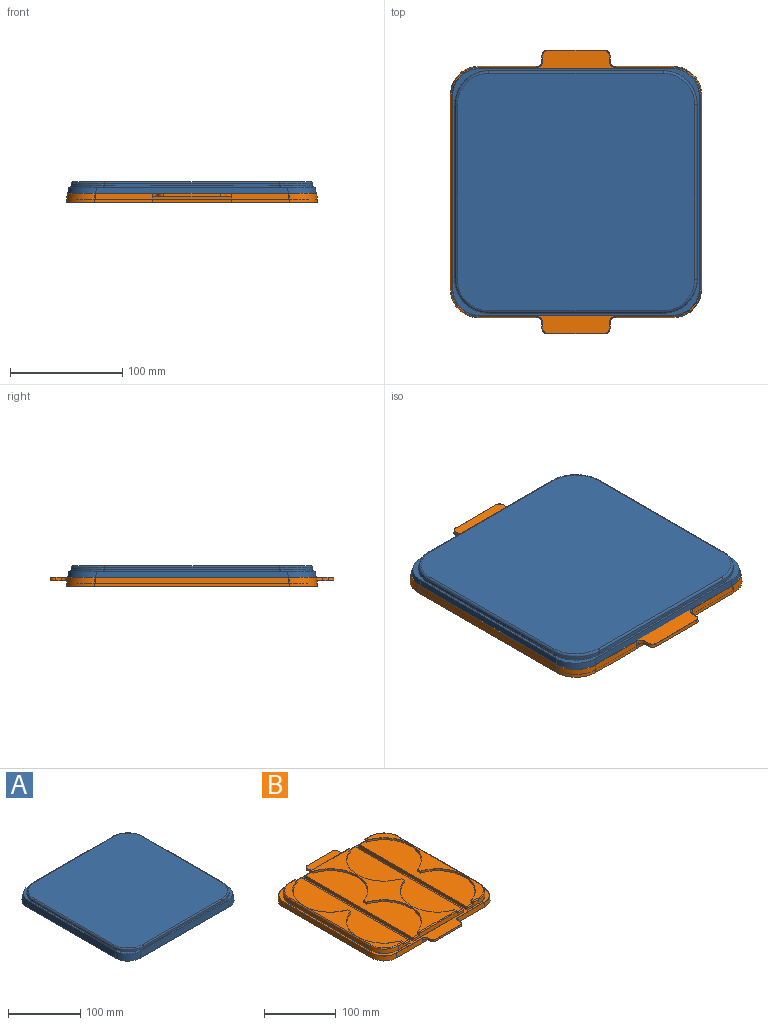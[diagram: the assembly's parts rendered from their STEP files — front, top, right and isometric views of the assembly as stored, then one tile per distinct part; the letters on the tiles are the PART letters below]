
ASSEMBLY  parts=2 mates=1
PART A: 45 faces, bbox 222.6x222.6x17.1 mm
  f0: plane 222.4x222.4mm, normal (0,0,-1), area 2110.5mm2, adj f2,f3,f4,f5,f6,f7,f8,f9
  f1: plane 220.09x220.09mm, normal (0,0,1), area 1993.2mm2, adj f2,f3,f4,f5,f6,f7,f8,f9
  f2: plane 172.67x11mm, normal (0,0.99,0.1), area 1897.1mm2, adj f0,f1,f6,f9
  f3: plane 172.67x11mm, normal (-0.99,0,0.1), area 1897.1mm2, adj f0,f1,f6,f7
  f4: plane 172.67x11mm, normal (0,-0.99,0.1), area 1897.1mm2, adj f0,f1,f7,f8
  f5: plane 172.67x11mm, normal (0.99,0,0.1), area 1897.1mm2, adj f0,f1,f8,f9
  f6: cylinder r=25mm len=26.13mm, axis (-0.1,0.1,-0.99), area 433.7mm2, adj f0,f1,f2,f3
  f7: cylinder r=25mm len=26.13mm, axis (-0.1,-0.1,-0.99), area 433.7mm2, adj f0,f1,f3,f4
  f8: cylinder r=25mm len=26.13mm, axis (0.1,-0.1,-0.99), area 433.7mm2, adj f0,f1,f4,f5
  f9: cylinder r=25mm len=26.13mm, axis (0.1,0.1,-0.99), area 433.7mm2, adj f0,f1,f2,f5
  f10: plane 156.38x3.21mm, normal (0,0.99,0.1), area 503.5mm2, adj f1,f15,f18,f24
  f11: plane 156.38x3.21mm, normal (-0.99,0,0.1), area 503.5mm2, adj f1,f15,f16,f25
  f12: plane 156.38x3.21mm, normal (0,-0.99,0.1), area 503.5mm2, adj f1,f16,f17,f21
  f13: plane 156.38x3.21mm, normal (0.99,0,0.1), area 503.5mm2, adj f1,f17,f18,f20
  f14: plane 211.4x211.4mm, normal (0,0,1), area 44026mm2, adj f19,f20,f21,f22,f23,f24,f25,f26
  f15: cylinder r=30mm len=30.31mm, axis (0.1,-0.1,0.99), area 154.5mm2, adj f1,f10,f11,f26
  f16: cylinder r=30mm len=30.31mm, axis (0.1,0.1,0.99), area 154.5mm2, adj f1,f11,f12,f23
  f17: cylinder r=30mm len=30.31mm, axis (-0.1,0.1,0.99), area 154.5mm2, adj f1,f12,f13,f19
  f18: cylinder r=30mm len=30.31mm, axis (-0.1,-0.1,0.99), area 154.5mm2, adj f1,f10,f13,f22
  f19: bspline ~29.84x29.84mm, area 131.3mm2, adj f14,f17,f20,f21
  f20: cylinder r=2mm len=155.71mm, axis (0,-1,0), area 456.6mm2, adj f13,f14,f19,f22
  f21: cylinder r=2mm len=155.71mm, axis (1,0,0), area 456.6mm2, adj f12,f14,f19,f23
  f22: bspline ~29.84x29.84mm, area 131.3mm2, adj f14,f18,f20,f24
  f23: bspline ~29.84x29.84mm, area 131.3mm2, adj f14,f16,f21,f25
  f24: cylinder r=2mm len=155.71mm, axis (1,0,0), area 456.6mm2, adj f10,f14,f22,f26
  f25: cylinder r=2mm len=155.71mm, axis (0,-1,0), area 456.6mm2, adj f11,f14,f23,f26
  f26: bspline ~29.84x29.84mm, area 131.3mm2, adj f14,f15,f24,f25
  f27: plane 215.59x215.59mm, normal (0,0,-1), area 1935.7mm2, adj f28,f29,f30,f31,f32,f33,f34,f35
  f28: plane 172.62x8.5mm, normal (0,-0.99,-0.1), area 1467.7mm2, adj f0,f27,f32,f35
  f29: plane 172.62x8.5mm, normal (0.99,0,-0.1), area 1467.7mm2, adj f0,f27,f32,f33
  f30: plane 172.62x8.5mm, normal (0,0.99,-0.1), area 1467.7mm2, adj f0,f27,f33,f34
  f31: plane 172.62x8.5mm, normal (-0.99,0,-0.1), area 1467.7mm2, adj f0,f27,f34,f35
  f32: cylinder r=22.5mm len=23.37mm, axis (-0.1,0.1,-0.99), area 301.6mm2, adj f0,f27,f28,f29
  f33: cylinder r=22.5mm len=23.37mm, axis (-0.1,-0.1,-0.99), area 301.6mm2, adj f0,f27,f29,f30
  f34: cylinder r=22.5mm len=23.37mm, axis (0.1,-0.1,-0.99), area 301.6mm2, adj f0,f27,f30,f31
  f35: cylinder r=22.5mm len=23.37mm, axis (0.1,0.1,-0.99), area 301.6mm2, adj f0,f27,f28,f31
  f36: plane 156.85x5mm, normal (0,-0.99,-0.1), area 785.9mm2, adj f27,f40,f41,f44
  f37: plane 156.85x5mm, normal (0.99,0,-0.1), area 785.9mm2, adj f27,f40,f41,f42
  f38: plane 156.85x5mm, normal (0,0.99,-0.1), area 785.9mm2, adj f27,f40,f42,f43
  f39: plane 156.85x5mm, normal (-0.99,0,-0.1), area 785.9mm2, adj f27,f40,f43,f44
  f40: plane 210.5x210.5mm, normal (0,0,-1), area 43669.6mm2, adj f36,f37,f38,f39,f41,f42,f43,f44
  f41: cylinder r=27.5mm len=28mm, axis (0.1,-0.1,0.99), area 216.8mm2, adj f27,f36,f37,f40
  f42: cylinder r=27.5mm len=28mm, axis (0.1,0.1,0.99), area 216.8mm2, adj f27,f37,f38,f40
  f43: cylinder r=27.5mm len=28mm, axis (-0.1,0.1,0.99), area 216.8mm2, adj f27,f38,f39,f40
  f44: cylinder r=27.5mm len=28mm, axis (-0.1,-0.1,0.99), area 216.8mm2, adj f27,f36,f39,f40
PART B: 298 faces, bbox 224x253.1x16.9 mm
  f0: plane 45.03x40.25mm, normal (0,0,-1), area 1431.9mm2, adj f1,f2,f130,f146,f213
  f1: plane 16.07x8.03mm, normal (-1,0,-0.09), area 100.6mm2, adj f0,f127,f139,f146,f163,f213
  f2: plane 40.95x5mm, normal (1,0,-0.09), area 203.8mm2, adj f0,f130,f139,f213
  f3: plane 93.03x40.25mm, normal (0,0,-1), area 2878.5mm2, adj f4,f5,f111,f116,f117,f211
  f4: plane 40.95x5mm, normal (1,0,-0.09), area 203.8mm2, adj f3,f111,f139,f211
  f5: plane 40.95x5mm, normal (-1,0,-0.09), area 203.8mm2, adj f3,f111,f139,f211
  f6: plane 16.07x8.03mm, normal (1,0,-0.09), area 100.6mm2, adj f7,f122,f135,f139,f160,f209
  f7: plane 45.03x40.25mm, normal (0,0,-1), area 1431.9mm2, adj f6,f8,f122,f133,f209
  f8: plane 40.95x5mm, normal (-1,0,-0.09), area 203.8mm2, adj f7,f133,f139,f209
  f9: plane 45.03x17.19mm, normal (0,0,-1), area 774.1mm2, adj f10,f11,f207,f283,f284,f285
  f10: plane 17.7x5mm, normal (-1,0,-0.09), area 87.5mm2, adj f9,f139,f207,f283
  f11: plane 17.7x5mm, normal (1,0,-0.09), area 87.5mm2, adj f9,f139,f207,f284
  f12: plane 93.03x17.19mm, normal (0,0,-1), area 1599.2mm2, adj f13,f14,f205,f280,f281,f282
  f13: plane 17.7x5mm, normal (1,0,-0.09), area 87.5mm2, adj f12,f139,f205,f281
  f14: plane 17.7x5mm, normal (-1,0,-0.09), area 87.5mm2, adj f12,f139,f205,f280
  f15: plane 17.7x5mm, normal (1,0,-0.09), area 87.5mm2, adj f16,f139,f203,f288
  f16: plane 45.03x17.19mm, normal (0,0,-1), area 774.1mm2, adj f15,f17,f203,f286,f287,f288
  f17: plane 17.7x5mm, normal (-1,0,-0.09), area 87.5mm2, adj f16,f139,f203,f286
  f18: plane 82.91x45.03mm, normal (0,0,-1), area 2873.8mm2, adj f19,f20,f121,f144,f145,f265,f266,f267
  f19: plane 83.43x8.03mm, normal (-1,0,-0.09), area 620.6mm2, adj f18,f121,f126,f139,f144,f265,f297
  f20: plane 83.4x5mm, normal (1,0,-0.09), area 417.3mm2, adj f18,f139,f266,f295
  f21: plane 93.03x82.91mm, normal (0,0,-1), area 5775.4mm2, adj f22,f23,f118,f119,f147,f148,f150,f151
  f22: plane 83.4x5mm, normal (1,0,-0.09), area 417.3mm2, adj f21,f139,f263,f294
  f23: plane 83.4x5mm, normal (-1,0,-0.09), area 417.3mm2, adj f21,f139,f262,f292
  f24: plane 83.43x8.03mm, normal (1,0,-0.09), area 620.6mm2, adj f25,f123,f124,f139,f152,f270,f291
  f25: plane 82.91x45.03mm, normal (0,0,-1), area 2873.8mm2, adj f24,f26,f123,f152,f153,f268,f269,f270
  f26: plane 83.4x5mm, normal (-1,0,-0.09), area 417.3mm2, adj f25,f139,f268,f289
  f27: plane 45.03x40.25mm, normal (0,0,-1), area 1431.9mm2, adj f28,f29,f120,f132,f206
  f28: plane 16.07x8.03mm, normal (-1,0,-0.09), area 100.6mm2, adj f27,f120,f136,f139,f162,f206
  f29: plane 40.95x5mm, normal (1,0,-0.09), area 203.8mm2, adj f27,f132,f139,f206
  f30: plane 93.03x40.25mm, normal (0,0,-1), area 2878.5mm2, adj f31,f32,f131,f149,f155,f204
  f31: plane 40.95x5mm, normal (1,0,-0.09), area 203.8mm2, adj f30,f131,f139,f204
  f32: plane 40.95x5mm, normal (-1,0,-0.09), area 203.8mm2, adj f30,f131,f139,f204
  f33: plane 16.07x8.03mm, normal (1,0,-0.09), area 100.6mm2, adj f34,f125,f139,f154,f161,f202
  f34: plane 45.03x40.25mm, normal (0,0,-1), area 1431.9mm2, adj f33,f35,f134,f154,f202
  f35: plane 40.95x5mm, normal (-1,0,-0.09), area 203.8mm2, adj f34,f134,f139,f202
  f36: plane 51.99x7.82mm, normal (0,1,0.09), area 402.8mm2, adj f56,f87,f178,f187,f224
  f37: plane 51.99x7.82mm, normal (0,-1,0.09), area 402.8mm2, adj f56,f89,f177,f186,f227
  f38: plane 51.99x7.82mm, normal (0,1,0.09), area 402.8mm2, adj f56,f88,f179,f188,f235
  f39: plane 99.37x6.45mm, normal (0,1,0.09), area 567.3mm2, adj f59,f69,f79,f81,f102,f105,f110,f249
  f40: plane 23.47x6.45mm, normal (0,1,0.09), area 112.2mm2, adj f58,f82,f86,f95,f106,f240
  f41: plane 99.37x6.45mm, normal (0,-1,0.09), area 567.3mm2, adj f67,f77,f79,f81,f101,f107,f109,f248
  f42: plane 23.47x6.45mm, normal (0,-1,0.09), area 112.2mm2, adj f60,f82,f85,f91,f108,f238
  f43: plane 211.78x48.25mm, normal (0,0,1), area 7810.2mm2, adj f58,f60,f61,f62,f63,f82,f106,f108
  f44: plane 211.78x48.25mm, normal (0,0,1), area 7810.2mm2, adj f69,f71,f72,f77,f78,f79,f105,f107
  f45: plane 23.47x6.45mm, normal (0,1,0.09), area 112.2mm2, adj f70,f80,f83,f100,f104,f243
  f46: plane 23.47x6.45mm, normal (0,-1,0.09), area 112.2mm2, adj f76,f80,f84,f96,f103,f245
  f47: plane 211.25x36.63mm, normal (0,0,1), area 2103.5mm2, adj f70,f76,f96,f97,f98,f99,f100,f259
  f48: plane 211.25x36.63mm, normal (0,0,1), area 2103.5mm2, adj f58,f60,f91,f92,f93,f94,f95,f250
  f49: plane 159.58x6.45mm, normal (-1,0,0.09), area 1029.3mm2, adj f83,f84,f98,f246
  f50: plane 159.58x6.45mm, normal (1,0,0.09), area 1029.3mm2, adj f85,f86,f93,f241
  f51: plane 211.25x74mm, normal (0,0,1), area 4962.1mm2, adj f59,f67,f69,f77,f109,f110,f253,f254
  f52: plane 252.04x222.03mm, normal (0,0,1), area 7538mm2, adj f79,f80,f81,f82,f214,f215,f216,f217
  f53: plane 173.99x7.82mm, normal (-1,0,0.09), area 1360mm2, adj f56,f87,f90,f220
  f54: plane 173.99x7.82mm, normal (1,0,0.09), area 1360mm2, adj f56,f88,f89,f231
  f55: plane 51.99x7.82mm, normal (0,-1,0.09), area 402.8mm2, adj f56,f90,f176,f184,f216
  f56: plane 223.8x223.8mm, normal (0,0,-1), area 2440.3mm2, adj f36,f37,f38,f53,f54,f55,f87,f88
  f57: plane 211.78x48.25mm, normal (0,0,1), area 7810.2mm2, adj f59,f64,f65,f66,f67,f81,f101,f102
  f58: plane 4.83x4.37mm, normal (-1,0,0.09), area 13.5mm2, adj f40,f43,f48,f63,f95,f106,f250
  f59: plane 4.83x4.37mm, normal (1,0,0.09), area 13.5mm2, adj f39,f51,f57,f64,f102,f110,f255
  f60: plane 4.83x4.37mm, normal (-1,0,0.09), area 13.5mm2, adj f42,f43,f48,f61,f91,f108,f252
  f61: cone r=52.25mm half-angle=5deg, axis (0,0,1), area 371.8mm2, adj f43,f60,f62,f252
  f62: plane 6.9x2.82mm, normal (-1,0,0.09), area 19mm2, adj f43,f61,f63,f251
  f63: cone r=52.25mm half-angle=5deg, axis (0,0,1), area 371.8mm2, adj f43,f58,f62,f250
  f64: cone r=52.25mm half-angle=5deg, axis (0,0,1), area 371.8mm2, adj f57,f59,f65,f255
  f65: plane 6.9x2.82mm, normal (1,0,0.09), area 19mm2, adj f57,f64,f66,f254
  f66: cone r=52.25mm half-angle=5deg, axis (0,0,1), area 371.8mm2, adj f57,f65,f67,f253
  f67: plane 4.83x4.37mm, normal (1,0,0.09), area 13.5mm2, adj f41,f51,f57,f66,f101,f109,f253
  f68: plane 211.78x48.25mm, normal (0,0,1), area 7810.2mm2, adj f70,f73,f74,f75,f76,f80,f103,f104
  f69: plane 4.83x4.37mm, normal (-1,0,0.09), area 13.5mm2, adj f39,f44,f51,f72,f105,f110,f256
  f70: plane 4.83x4.37mm, normal (1,0,0.09), area 13.5mm2, adj f45,f47,f68,f73,f100,f104,f259
  f71: plane 6.9x2.82mm, normal (-1,0,0.09), area 19mm2, adj f44,f72,f78,f257
  f72: cone r=52.25mm half-angle=5deg, axis (0,0,1), area 371.8mm2, adj f44,f69,f71,f256
  f73: cone r=52.25mm half-angle=5deg, axis (0,0,1), area 371.8mm2, adj f68,f70,f74,f259
  f74: plane 6.9x2.82mm, normal (1,0,0.09), area 19mm2, adj f68,f73,f75,f260
  f75: cone r=52.25mm half-angle=5deg, axis (0,0,1), area 371.8mm2, adj f68,f74,f76,f261
  f76: plane 4.83x4.37mm, normal (1,0,0.09), area 13.5mm2, adj f46,f47,f68,f75,f96,f103,f261
  f77: plane 4.83x4.37mm, normal (-1,0,0.09), area 13.5mm2, adj f41,f44,f51,f78,f107,f109,f258
  f78: cone r=52.25mm half-angle=5deg, axis (0,0,1), area 371.8mm2, adj f44,f71,f77,f258
  f79: plane 215.77x5.01mm, normal (-1,0,0.09), area 1078.1mm2, adj f39,f41,f44,f52,f105,f107,f248,f249
  f80: plane 215.77x5.01mm, normal (1,0,0.09), area 1078.1mm2, adj f45,f46,f52,f68,f103,f104,f243,f245
  f81: plane 215.77x5.01mm, normal (1,0,0.09), area 1078.1mm2, adj f39,f41,f52,f57,f101,f102,f248,f249
  f82: plane 215.77x5.01mm, normal (-1,0,0.09), area 1078.1mm2, adj f40,f42,f43,f52,f106,f108,f238,f240
  f83: cylinder r=28mm len=28.55mm, axis (0.09,-0.09,0.99), area 286.1mm2, adj f45,f49,f99,f244
  f84: cylinder r=28mm len=28.55mm, axis (0.09,0.09,0.99), area 286.1mm2, adj f46,f49,f97,f247
  f85: cylinder r=28mm len=28.55mm, axis (-0.09,0.09,0.99), area 286.1mm2, adj f42,f50,f92,f239
  f86: cylinder r=28mm len=28.55mm, axis (-0.09,-0.09,0.99), area 286.1mm2, adj f40,f50,f94,f242
  f87: cylinder r=25mm len=25.67mm, axis (0.09,-0.09,0.99), area 308mm2, adj f36,f53,f56,f222
  f88: cylinder r=25mm len=25.67mm, axis (-0.09,-0.09,0.99), area 308mm2, adj f38,f54,f56,f233
  f89: cylinder r=25mm len=25.67mm, axis (-0.09,0.09,0.99), area 308mm2, adj f37,f54,f56,f229
  f90: cylinder r=25mm len=25.67mm, axis (0.09,0.09,0.99), area 308mm2, adj f53,f55,f56,f218
  f91: cylinder r=1.5mm len=10.35mm, axis (1,0,0), area 22.9mm2, adj f42,f48,f60,f92
  f92: bspline ~27.89x27.89mm, area 94mm2, adj f48,f85,f91,f93
  f93: cylinder r=1.5mm len=158.45mm, axis (0,-1,0), area 352.6mm2, adj f48,f50,f92,f94
  f94: bspline ~27.89x27.89mm, area 94mm2, adj f48,f86,f93,f95
  f95: cylinder r=1.5mm len=10.35mm, axis (1,0,0), area 22.9mm2, adj f40,f48,f58,f94
  f96: cylinder r=1.5mm len=10.35mm, axis (1,0,0), area 22.9mm2, adj f46,f47,f76,f97
  f97: bspline ~27.89x27.89mm, area 94mm2, adj f47,f84,f96,f98
  f98: cylinder r=1.5mm len=158.45mm, axis (0,-1,0), area 352.6mm2, adj f47,f49,f97,f99
  f99: bspline ~27.89x27.89mm, area 94mm2, adj f47,f83,f98,f100
  f100: cylinder r=1.5mm len=10.35mm, axis (1,0,0), area 22.9mm2, adj f45,f47,f70,f99
  f101: cylinder r=1.5mm len=12.12mm, axis (-1,0,0), area 26.7mm2, adj f41,f57,f67,f81
  f102: cylinder r=1.5mm len=12.12mm, axis (-1,0,0), area 26.7mm2, adj f39,f57,f59,f81
  f103: cylinder r=1.5mm len=12.12mm, axis (-1,0,0), area 26.7mm2, adj f46,f68,f76,f80
  f104: cylinder r=1.5mm len=12.12mm, axis (-1,0,0), area 26.7mm2, adj f45,f68,f70,f80
  f105: cylinder r=1.5mm len=12.12mm, axis (-1,0,0), area 26.7mm2, adj f39,f44,f69,f79
  f106: cylinder r=1.5mm len=12.12mm, axis (-1,0,0), area 26.7mm2, adj f40,f43,f58,f82
  f107: cylinder r=1.5mm len=12.12mm, axis (-1,0,0), area 26.7mm2, adj f41,f44,f77,f79
  f108: cylinder r=1.5mm len=12.12mm, axis (-1,0,0), area 26.7mm2, adj f42,f43,f60,f82
  f109: cylinder r=1.5mm len=74.24mm, axis (1,0,0), area 164.9mm2, adj f41,f51,f67,f77
  f110: cylinder r=1.5mm len=74.24mm, axis (1,0,0), area 164.9mm2, adj f39,f51,f59,f69
  f111: plane 93.93x8.03mm, normal (0,-1,-0.09), area 672.4mm2, adj f3,f4,f5,f116,f117,f138,f139
  f112: plane 93.03x17.19mm, normal (0,0,-1), area 1599.2mm2, adj f156,f158,f210,f274,f275,f276
  f113: plane 45.03x17.19mm, normal (0,0,-1), area 774.1mm2, adj f137,f159,f212,f277,f278,f279
  f114: plane 17.7x5mm, normal (1,0,-0.09), area 87.5mm2, adj f115,f139,f208,f273
  f115: plane 45.03x17.19mm, normal (0,0,-1), area 774.1mm2, adj f114,f157,f208,f271,f272,f273
  f116: cone r=55.24mm half-angle=5deg, axis (0,0,1), area 157.2mm2, adj f3,f111,f117,f138
  f117: cone r=55.24mm half-angle=5deg, axis (0,0,1), area 157.2mm2, adj f3,f111,f116,f138
  f118: cone r=55.24mm half-angle=5deg, axis (0,0,1), area 159.1mm2, adj f21,f119,f128,f148
  f119: cone r=55.24mm half-angle=5deg, axis (0,0,1), area 159.1mm2, adj f21,f118,f128,f150
  f120: cone r=55.24mm half-angle=5deg, axis (0,0,1), area 141.2mm2, adj f27,f28,f132,f136
  f121: cone r=55.24mm half-angle=5deg, axis (0,0,1), area 143.2mm2, adj f18,f19,f126,f145
  f122: cone r=55.24mm half-angle=5deg, axis (0,0,1), area 141.2mm2, adj f6,f7,f133,f135
  f123: cone r=55.24mm half-angle=5deg, axis (0,0,1), area 143.2mm2, adj f24,f25,f124,f153
  f124: plane 66.09x32.5mm, normal (0,0,-1), area 815.8mm2, adj f24,f123,f152,f153
  f125: plane 31.3x31.3mm, normal (0,0,-1), area 218.6mm2, adj f33,f134,f154,f161
  f126: plane 66.09x32.5mm, normal (0,0,-1), area 815.8mm2, adj f19,f121,f144,f145
  f127: plane 31.3x31.3mm, normal (0,0,-1), area 218.6mm2, adj f1,f130,f146,f163
  f128: plane 76.61x68.5mm, normal (0,0,-1), area 1880.2mm2, adj f118,f119,f147,f148,f150,f151
  f129: plane 66.09x36.56mm, normal (0,0,-1), area 820.9mm2, adj f131,f149,f155
  f130: plane 21.02x8.03mm, normal (0,-1,-0.09), area 125mm2, adj f0,f2,f127,f139,f146,f163
  f131: plane 93.93x8.03mm, normal (0,1,-0.09), area 672.4mm2, adj f30,f31,f32,f129,f139,f149,f155
  f132: plane 21.02x8.03mm, normal (0,1,-0.09), area 125mm2, adj f27,f29,f120,f136,f139,f162
  f133: plane 21.02x8.03mm, normal (0,-1,-0.09), area 125mm2, adj f7,f8,f122,f135,f139,f160
  f134: plane 21.02x8.03mm, normal (0,1,-0.09), area 125mm2, adj f34,f35,f125,f139,f154,f161
  f135: plane 31.3x31.3mm, normal (0,0,-1), area 218.6mm2, adj f6,f122,f133,f160
  f136: plane 31.3x31.3mm, normal (0,0,-1), area 218.6mm2, adj f28,f120,f132,f162
  f137: plane 17.7x5mm, normal (-1,0,-0.09), area 87.5mm2, adj f113,f139,f212,f279
  f138: plane 66.09x36.56mm, normal (0,0,-1), area 820.9mm2, adj f111,f116,f117
  f139: plane 216.9x216.9mm, normal (0,0,-1), area 9672.4mm2, adj f1,f2,f4,f5,f6,f8,f10,f11
  f140: plane 173.94x5mm, normal (1,0,-0.09), area 870.8mm2, adj f56,f139,f164,f167
  f141: plane 173.94x5mm, normal (0,-1,-0.09), area 870.8mm2, adj f56,f139,f164,f165
  f142: plane 173.94x5mm, normal (-1,0,-0.09), area 870.8mm2, adj f56,f139,f165,f166
  f143: plane 173.94x5mm, normal (0,1,-0.09), area 870.8mm2, adj f56,f139,f166,f167
  f144: cone r=55.24mm half-angle=5deg, axis (0,0,1), area 143.2mm2, adj f18,f19,f126,f145
  f145: plane 3x2.96mm, normal (1,0,-0.09), area 8.4mm2, adj f18,f121,f126,f144
  f146: cone r=55.24mm half-angle=5deg, axis (0,0,1), area 141.2mm2, adj f0,f1,f127,f130
  f147: cone r=55.24mm half-angle=5deg, axis (0,0,1), area 159.1mm2, adj f21,f128,f148,f151
  f148: plane 3x2.96mm, normal (-1,0,-0.09), area 8.4mm2, adj f21,f118,f128,f147
  f149: cone r=55.24mm half-angle=5deg, axis (0,0,1), area 157.2mm2, adj f30,f129,f131,f155
  f150: plane 3x2.96mm, normal (1,0,-0.09), area 8.4mm2, adj f21,f119,f128,f151
  f151: cone r=55.24mm half-angle=5deg, axis (0,0,1), area 159.1mm2, adj f21,f128,f147,f150
  f152: cone r=55.24mm half-angle=5deg, axis (0,0,1), area 143.2mm2, adj f24,f25,f124,f153
  f153: plane 3x2.96mm, normal (-1,0,-0.09), area 8.4mm2, adj f25,f123,f124,f152
  f154: cone r=55.24mm half-angle=5deg, axis (0,0,1), area 141.2mm2, adj f33,f34,f125,f134
  f155: cone r=55.24mm half-angle=5deg, axis (0,0,1), area 157.2mm2, adj f30,f129,f131,f149
  f156: plane 17.7x5mm, normal (1,0,-0.09), area 87.5mm2, adj f112,f139,f210,f276
  f157: plane 17.7x5mm, normal (-1,0,-0.09), area 87.5mm2, adj f115,f139,f208,f271
  f158: plane 17.7x5mm, normal (-1,0,-0.09), area 87.5mm2, adj f112,f139,f210,f274
  f159: plane 17.7x5mm, normal (1,0,-0.09), area 87.5mm2, adj f113,f139,f212,f277
  f160: cylinder r=25mm len=25.68mm, axis (0.09,-0.09,0.99), area 315mm2, adj f6,f133,f135,f139
  f161: cylinder r=25mm len=25.68mm, axis (0.09,0.09,0.99), area 315mm2, adj f33,f125,f134,f139
  f162: cylinder r=25mm len=25.68mm, axis (-0.09,0.09,0.99), area 315mm2, adj f28,f132,f136,f139
  f163: cylinder r=25mm len=25.68mm, axis (-0.09,-0.09,0.99), area 315mm2, adj f1,f127,f130,f139
  f164: cylinder r=22mm len=22.42mm, axis (0.09,-0.09,0.99), area 173.3mm2, adj f56,f139,f140,f141
  f165: cylinder r=22mm len=22.42mm, axis (-0.09,-0.09,0.99), area 173.3mm2, adj f56,f139,f141,f142
  f166: cylinder r=22mm len=22.42mm, axis (-0.09,0.09,0.99), area 173.3mm2, adj f56,f139,f142,f143
  f167: cylinder r=22mm len=22.42mm, axis (0.09,0.09,0.99), area 173.3mm2, adj f56,f139,f140,f143
  f168: plane 5.35x2.82mm, normal (-0.99,0,0.1), area 14.4mm2, adj f170,f178,f182,f228
  f169: plane 5.35x2.82mm, normal (0.99,0,0.1), area 14.4mm2, adj f170,f179,f183,f236
  f170: plane 70.59x15.05mm, normal (0,0,-1), area 912.7mm2, adj f168,f169,f171,f178,f179,f182,f183,f189
  f171: plane 50.69x2.82mm, normal (0,0.99,0.1), area 142.9mm2, adj f170,f182,f183,f232
  f172: plane 5.35x2.82mm, normal (-0.99,0,0.1), area 14.4mm2, adj f175,f176,f180,f215
  f173: plane 50.69x2.82mm, normal (0,-0.99,0.1), area 142.9mm2, adj f175,f180,f181,f219
  f174: plane 5.35x2.82mm, normal (0.99,0,0.1), area 14.4mm2, adj f175,f177,f181,f223
  f175: plane 70.59x15.05mm, normal (0,0,-1), area 912.7mm2, adj f172,f173,f174,f176,f177,f180,f181,f185
  f176: cylinder r=5mm len=5.3mm, axis (0.1,0.09,0.99), area 22.3mm2, adj f55,f172,f175,f214
  f177: cylinder r=5mm len=5.3mm, axis (-0.1,0.09,0.99), area 22.3mm2, adj f37,f174,f175,f225
  f178: cylinder r=5mm len=5.3mm, axis (-0.1,0.09,-0.99), area 22.3mm2, adj f36,f168,f170,f226
  f179: cylinder r=5mm len=5.3mm, axis (0.1,0.09,-0.99), area 22.3mm2, adj f38,f169,f170,f237
  f180: cylinder r=5mm len=5.29mm, axis (0.1,0.1,0.99), area 22.3mm2, adj f172,f173,f175,f217
  f181: cylinder r=5mm len=5.29mm, axis (-0.1,0.1,0.99), area 22.3mm2, adj f173,f174,f175,f221
  f182: cylinder r=5mm len=5.29mm, axis (0.1,-0.1,0.99), area 22.3mm2, adj f168,f170,f171,f230
  f183: cylinder r=5mm len=5.29mm, axis (-0.1,-0.1,0.99), area 22.3mm2, adj f169,f170,f171,f234
  f184: plane 5x0.7mm, normal (1,0,-0.05), area 1.8mm2, adj f55,f56,f185
  f185: plane 71.12x5mm, normal (0,-1,-0.05), area 354.8mm2, adj f56,f175,f184,f186
  f186: plane 5x0.7mm, normal (-1,0,-0.05), area 1.8mm2, adj f37,f56,f185
  f187: plane 5x0.7mm, normal (1,0,-0.05), area 1.8mm2, adj f36,f56,f189
  f188: plane 5x0.7mm, normal (-1,0,-0.05), area 1.8mm2, adj f38,f56,f189
  f189: plane 71.12x5mm, normal (0,1,-0.05), area 354.8mm2, adj f56,f170,f187,f188
  f190: plane 45.3x4.72mm, normal (0,-1,-0.05), area 212mm2, adj f139,f286,f287,f288
  f191: plane 45.3x4.72mm, normal (0,1,-0.05), area 212mm2, adj f139,f289,f290,f291
  f192: plane 93.3x4.72mm, normal (0,-1,-0.05), area 438.6mm2, adj f139,f280,f281,f282
  f193: plane 93.3x4.72mm, normal (0,1,-0.05), area 438.6mm2, adj f139,f292,f293,f294
  f194: plane 45.3x4.72mm, normal (0,-1,-0.05), area 212mm2, adj f139,f283,f284,f285
  f195: plane 45.3x4.72mm, normal (0,1,-0.05), area 212mm2, adj f139,f295,f296,f297
  f196: plane 45.3x4.72mm, normal (0,-1,-0.05), area 212mm2, adj f139,f268,f269,f270
  f197: plane 45.3x4.72mm, normal (0,1,-0.05), area 212mm2, adj f139,f271,f272,f273
  f198: plane 93.3x4.72mm, normal (0,-1,-0.05), area 438.6mm2, adj f139,f262,f263,f264
  f199: plane 93.3x4.72mm, normal (0,1,-0.05), area 438.6mm2, adj f139,f274,f275,f276
  f200: plane 45.3x4.72mm, normal (0,-1,-0.05), area 212mm2, adj f139,f265,f266,f267
  f201: plane 45.3x4.72mm, normal (0,1,-0.05), area 212mm2, adj f139,f277,f278,f279
  f202: plane 45.9x5mm, normal (0,-1,-0.05), area 227.6mm2, adj f33,f34,f35,f139
  f203: plane 45.9x5mm, normal (0,1,-0.05), area 227.6mm2, adj f15,f16,f17,f139
  f204: plane 93.9x5mm, normal (0,-1,-0.05), area 468mm2, adj f30,f31,f32,f139
  f205: plane 93.9x5mm, normal (0,1,-0.05), area 468mm2, adj f12,f13,f14,f139
  f206: plane 45.9x5mm, normal (0,-1,-0.05), area 227.6mm2, adj f27,f28,f29,f139
  f207: plane 45.9x5mm, normal (0,1,-0.05), area 227.6mm2, adj f9,f10,f11,f139
  f208: plane 45.9x5mm, normal (0,-1,-0.05), area 227.6mm2, adj f114,f115,f139,f157
  f209: plane 45.9x5mm, normal (0,1,-0.05), area 227.6mm2, adj f6,f7,f8,f139
  f210: plane 93.9x5mm, normal (0,-1,-0.05), area 468mm2, adj f112,f139,f156,f158
  f211: plane 93.9x5mm, normal (0,1,-0.05), area 468mm2, adj f3,f4,f5,f139
  f212: plane 45.9x5mm, normal (0,-1,-0.05), area 227.6mm2, adj f113,f137,f139,f159
  f213: plane 45.9x5mm, normal (0,1,-0.05), area 227.6mm2, adj f0,f1,f2,f139
  f214: bspline ~5.18x5.17mm, area 2.3mm2, adj f52,f176,f215,f216
  f215: cylinder r=0.2mm len=5.06mm, axis (0,1,0), area 1.5mm2, adj f52,f172,f214,f217
  f216: cylinder r=0.2mm len=51.31mm, axis (-1,0,0), area 15.2mm2, adj f52,f55,f214,f218
  f217: bspline ~4.97x4.97mm, area 2.2mm2, adj f52,f180,f215,f219
  f218: bspline ~24.91x24.91mm, area 11.4mm2, adj f52,f90,f216,f220
  f219: cylinder r=0.2mm len=50.09mm, axis (1,0,0), area 14.7mm2, adj f52,f173,f217,f221
  f220: cylinder r=0.2mm len=172.62mm, axis (0,-1,0), area 51.2mm2, adj f52,f53,f218,f222
  f221: bspline ~4.97x4.97mm, area 2.2mm2, adj f52,f181,f219,f223
  f222: bspline ~24.91x24.91mm, area 11.4mm2, adj f52,f87,f220,f224
  f223: cylinder r=0.2mm len=5.06mm, axis (0,1,0), area 1.5mm2, adj f52,f174,f221,f225
  f224: cylinder r=0.2mm len=51.31mm, axis (-1,0,0), area 15.2mm2, adj f36,f52,f222,f226
  f225: bspline ~5.18x5.17mm, area 2.3mm2, adj f52,f177,f223,f227
  f226: bspline ~5.18x5.17mm, area 2.3mm2, adj f52,f178,f224,f228
  f227: cylinder r=0.2mm len=51.31mm, axis (-1,0,0), area 15.2mm2, adj f37,f52,f225,f229
  f228: cylinder r=0.2mm len=5.06mm, axis (0,-1,0), area 1.5mm2, adj f52,f168,f226,f230
  f229: bspline ~24.91x24.91mm, area 11.4mm2, adj f52,f89,f227,f231
  f230: bspline ~4.97x4.97mm, area 2.2mm2, adj f52,f182,f228,f232
  f231: cylinder r=0.2mm len=172.62mm, axis (0,-1,0), area 51.2mm2, adj f52,f54,f229,f233
  f232: cylinder r=0.2mm len=50.09mm, axis (1,0,0), area 14.7mm2, adj f52,f171,f230,f234
  f233: bspline ~24.91x24.91mm, area 11.4mm2, adj f52,f88,f231,f235
  f234: bspline ~4.97x4.97mm, area 2.2mm2, adj f52,f183,f232,f236
  f235: cylinder r=0.2mm len=51.31mm, axis (-1,0,0), area 15.2mm2, adj f38,f52,f233,f237
  f236: cylinder r=0.2mm len=5.06mm, axis (0,-1,0), area 1.5mm2, adj f52,f169,f234,f237
  f237: bspline ~5.18x5.17mm, area 2.3mm2, adj f52,f179,f235,f236
  f238: cylinder r=0.2mm len=23.49mm, axis (1,0,0), area 7mm2, adj f42,f52,f82,f239
  f239: bspline ~28.09x28.09mm, area 12.8mm2, adj f52,f85,f238,f241
  f240: cylinder r=0.2mm len=23.49mm, axis (1,0,0), area 7mm2, adj f40,f52,f82,f242
  f241: cylinder r=0.2mm len=159.58mm, axis (0,-1,0), area 47.3mm2, adj f50,f52,f239,f242
  f242: bspline ~28.09x28.09mm, area 12.8mm2, adj f52,f86,f240,f241
  f243: cylinder r=0.2mm len=23.49mm, axis (1,0,0), area 7mm2, adj f45,f52,f80,f244
  f244: bspline ~28.09x28.09mm, area 12.8mm2, adj f52,f83,f243,f246
  f245: cylinder r=0.2mm len=23.49mm, axis (1,0,0), area 7mm2, adj f46,f52,f80,f247
  f246: cylinder r=0.2mm len=159.58mm, axis (0,-1,0), area 47.3mm2, adj f49,f52,f244,f247
  f247: bspline ~28.09x28.09mm, area 12.8mm2, adj f52,f84,f245,f246
  f248: cylinder r=0.2mm len=99.4mm, axis (1,0,0), area 29.5mm2, adj f41,f52,f79,f81
  f249: cylinder r=0.2mm len=99.4mm, axis (1,0,0), area 29.5mm2, adj f39,f52,f79,f81
  f250: torus R=52.43mm, axis (0,0,1), area 39.1mm2, adj f48,f58,f63,f251
  f251: cylinder r=0.2mm len=6.54mm, axis (0,1,0), area 1.9mm2, adj f48,f62,f250,f252
  f252: torus R=52.43mm, axis (0,0,1), area 39.1mm2, adj f48,f60,f61,f251
  f253: torus R=52.43mm, axis (0,0,1), area 39.1mm2, adj f51,f66,f67,f254
  f254: cylinder r=0.2mm len=6.54mm, axis (0,1,0), area 1.9mm2, adj f51,f65,f253,f255
  f255: torus R=52.43mm, axis (0,0,1), area 39.1mm2, adj f51,f59,f64,f254
  f256: torus R=52.43mm, axis (0,0,1), area 39.1mm2, adj f51,f69,f72,f257
  f257: cylinder r=0.2mm len=6.54mm, axis (0,1,0), area 1.9mm2, adj f51,f71,f256,f258
  f258: torus R=52.43mm, axis (0,0,1), area 39.1mm2, adj f51,f77,f78,f257
  f259: torus R=52.43mm, axis (0,0,1), area 39.1mm2, adj f47,f70,f73,f260
  f260: cylinder r=0.2mm len=6.54mm, axis (0,1,0), area 1.9mm2, adj f47,f74,f259,f261
  f261: torus R=52.43mm, axis (0,0,1), area 39.1mm2, adj f47,f75,f76,f260
  f262: cylinder r=0.3mm len=5.02mm, axis (-0.09,-0.05,0.99), area 2.3mm2, adj f21,f23,f139,f198,f264
  f263: cylinder r=0.3mm len=5.02mm, axis (0.09,-0.05,0.99), area 2.3mm2, adj f21,f22,f139,f198,f264
  f264: cylinder r=0.3mm len=93.03mm, axis (-1,0,0), area 42.3mm2, adj f21,f198,f262,f263
  f265: cylinder r=0.3mm len=5.02mm, axis (0.09,0.05,-0.99), area 2.3mm2, adj f18,f19,f139,f200,f267
  f266: cylinder r=0.3mm len=5.02mm, axis (0.09,-0.05,0.99), area 2.3mm2, adj f18,f20,f139,f200,f267
  f267: cylinder r=0.3mm len=45.03mm, axis (-1,0,0), area 20.4mm2, adj f18,f200,f265,f266
  f268: cylinder r=0.3mm len=5.02mm, axis (-0.09,-0.05,0.99), area 2.3mm2, adj f25,f26,f139,f196,f269
  f269: cylinder r=0.3mm len=45.03mm, axis (-1,0,0), area 20.4mm2, adj f25,f196,f268,f270
  f270: cylinder r=0.3mm len=5.02mm, axis (-0.09,0.05,-0.99), area 2.3mm2, adj f24,f25,f139,f196,f269
  f271: cylinder r=0.3mm len=5.02mm, axis (-0.09,0.05,0.99), area 2.3mm2, adj f115,f139,f157,f197,f272
  f272: cylinder r=0.3mm len=45.03mm, axis (-1,0,0), area 20.4mm2, adj f115,f197,f271,f273
  f273: cylinder r=0.3mm len=5.02mm, axis (-0.09,-0.05,-0.99), area 2.3mm2, adj f114,f115,f139,f197,f272
  f274: cylinder r=0.3mm len=5.02mm, axis (-0.09,0.05,0.99), area 2.3mm2, adj f112,f139,f158,f199,f275
  f275: cylinder r=0.3mm len=93.03mm, axis (-1,0,0), area 42.3mm2, adj f112,f199,f274,f276
  f276: cylinder r=0.3mm len=5.02mm, axis (0.09,0.05,0.99), area 2.3mm2, adj f112,f139,f156,f199,f275
  f277: cylinder r=0.3mm len=5.02mm, axis (0.09,0.05,0.99), area 2.3mm2, adj f113,f139,f159,f201,f278
  f278: cylinder r=0.3mm len=45.03mm, axis (-1,0,0), area 20.4mm2, adj f113,f201,f277,f279
  f279: cylinder r=0.3mm len=5.02mm, axis (0.09,-0.05,-0.99), area 2.3mm2, adj f113,f137,f139,f201,f278
  f280: cylinder r=0.3mm len=5.02mm, axis (-0.09,-0.05,0.99), area 2.3mm2, adj f12,f14,f139,f192,f282
  f281: cylinder r=0.3mm len=5.02mm, axis (0.09,-0.05,0.99), area 2.3mm2, adj f12,f13,f139,f192,f282
  f282: cylinder r=0.3mm len=93.03mm, axis (-1,0,0), area 42.3mm2, adj f12,f192,f280,f281
  f283: cylinder r=0.3mm len=5.02mm, axis (0.09,0.05,-0.99), area 2.3mm2, adj f9,f10,f139,f194,f285
  f284: cylinder r=0.3mm len=5.02mm, axis (0.09,-0.05,0.99), area 2.3mm2, adj f9,f11,f139,f194,f285
  f285: cylinder r=0.3mm len=45.03mm, axis (-1,0,0), area 20.4mm2, adj f9,f194,f283,f284
  f286: cylinder r=0.3mm len=5.02mm, axis (-0.09,-0.05,0.99), area 2.3mm2, adj f16,f17,f139,f190,f287
  f287: cylinder r=0.3mm len=45.03mm, axis (-1,0,0), area 20.4mm2, adj f16,f190,f286,f288
  f288: cylinder r=0.3mm len=5.02mm, axis (-0.09,0.05,-0.99), area 2.3mm2, adj f15,f16,f139,f190,f287
  f289: cylinder r=0.3mm len=5.02mm, axis (-0.09,0.05,0.99), area 2.3mm2, adj f25,f26,f139,f191,f290
  f290: cylinder r=0.3mm len=45.03mm, axis (-1,0,0), area 20.4mm2, adj f25,f191,f289,f291
  f291: cylinder r=0.3mm len=5.02mm, axis (-0.09,-0.05,-0.99), area 2.3mm2, adj f24,f25,f139,f191,f290
  f292: cylinder r=0.3mm len=5.02mm, axis (-0.09,0.05,0.99), area 2.3mm2, adj f21,f23,f139,f193,f293
  f293: cylinder r=0.3mm len=93.03mm, axis (-1,0,0), area 42.3mm2, adj f21,f193,f292,f294
  f294: cylinder r=0.3mm len=5.02mm, axis (0.09,0.05,0.99), area 2.3mm2, adj f21,f22,f139,f193,f293
  f295: cylinder r=0.3mm len=5.02mm, axis (0.09,0.05,0.99), area 2.3mm2, adj f18,f20,f139,f195,f296
  f296: cylinder r=0.3mm len=45.03mm, axis (-1,0,0), area 20.4mm2, adj f18,f195,f295,f297
  f297: cylinder r=0.3mm len=5.02mm, axis (0.09,-0.05,-0.99), area 2.3mm2, adj f18,f19,f139,f195,f296
PLACE A t=(-88.62,-20.55,40.41)mm
PLACE B t=(-88.62,-20.55,53.91)mm
MATE fastened A.f40 <-> B.f51  axis (0,0,-1) through (-88.62,-20.55,53.91)mm
